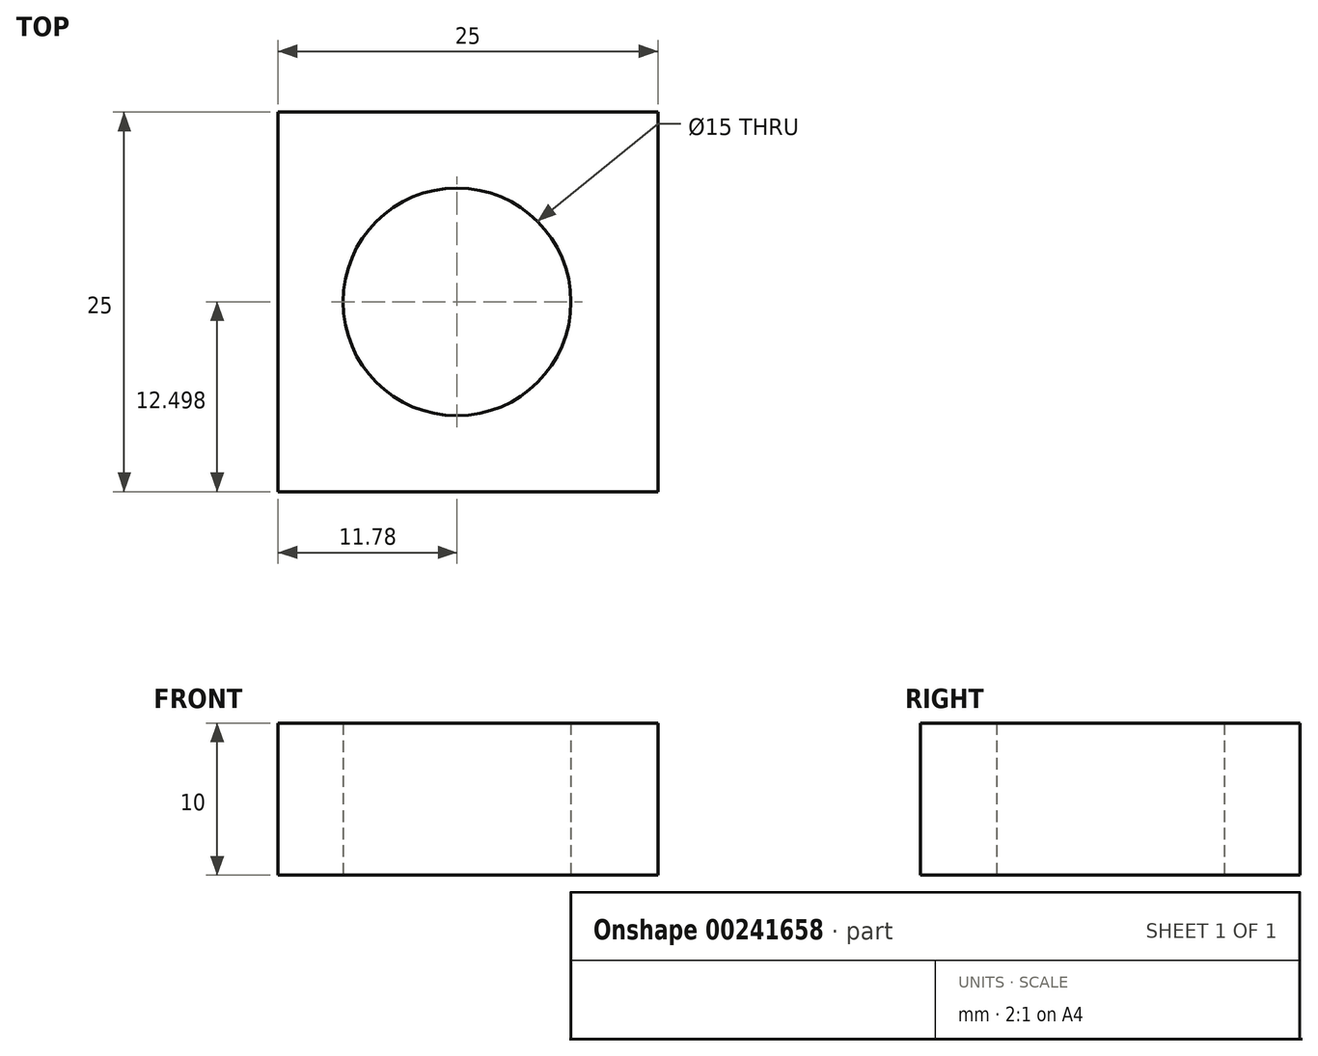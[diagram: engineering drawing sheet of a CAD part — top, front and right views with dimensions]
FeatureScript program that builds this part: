
annotation { "Feature Type Name" : "Feature", "Feature Type Description" : "" }
export const myFeature = defineFeature(function(context is Context, id is Id, definition is map)
    precondition{}
    {
        {
            var Q0;
            Q0=qCreatedBy(makeId("Top.planeOp"),FACE);
            var sketch = newSketch(context, id + "F0", { "sketchPlane" : qUnion([Q0])});
            skLineSegment(sketch, "E0.bottom", {"start": v(-11.78, 17.35) * mm, "end": v(13.22, 17.35) * mm});
            skLineSegment(sketch, "E0.top", {"start": v(-11.78, -7.65) * mm, "end": v(13.22, -7.65) * mm});
            skLineSegment(sketch, "E0.left", {"start": v(-11.78, 17.35) * mm, "end": v(-11.78, -7.65) * mm});
            skLineSegment(sketch, "E0.right", {"start": v(13.22, 17.35) * mm, "end": v(13.22, -7.65) * mm});
            skCircle(sketch, "E1", {"center": v(0, 4.85) * mm, "radius": 7.5 * mm});
            skSolve(sketch);
        }
        {
            var Q0;
            Q0=makeQuery(id+"F0.imprint","IMPRINT",FACE,{"disambiguationData":[TD([[makeQuery(id+"F0.imprint","IMPRINT",EDGE,{"derivedFrom":sQuery(id+"F0.wireOp",EDGE,"E0.bottom")}),-1.0]])]});
            extrude(context, id + "F1", {"entities" : qUnion([Q0]), "depth" : 10 * mm});
        }
    });
